# Revit family: BuroSeating_Konfurb Keen 5 Star
name_source: partatom
category: Furniture
units: mm (PartAtom-declared; Revit-internal decimal feet)

## family parameters
Always vertical = Yes
Cut with Voids When Loaded = No
OmniClass Number = 23.40.20.00
OmniClass Title = General Furniture and Specialties
Render Appearance Source = Family Geometry
Room Calculation Point = No
Shared = No
Work Plane-Based = No

## types (4) — shared parameters
Arm Finish = BuroSeating_Plastic_Black
Assembly Code = E2020
Back Finish = BuroSeating_Plastic_Navy
Base Finish = BuroSeating_Metal_PowderCoat_White
Caster Finish = BuroSeating_Plastic_Black
Cylinder Finish = BuroSeating_Metal_PowderCoat_White
Frame Finish = BuroSeating_Plastic_Silver
FrameMaterial = BuroSeating_Metal_PowderCoat_White
Glide Finish = BuroSeating_Plastic_Black
Leg Finish = BuroSeating_Plastic_Silver
Manufacturer = Buro Seating
Mechanism Finish = BuroSeating_Plastic_Black
ProductGroup = Konfurb Keen
ProductPageURL AU = https://buroseating.com
ProductRange = Konfurb
Ring Finish = BuroSeating_Metal_PowderCoat_White
Seat Finish = BuroSeating_Plastic_Navy
SeatDepth = 450 mm  [stored 1.47638 ft]
SeatWidth = 450 mm  [stored 1.47638 ft]
Supports Finish = BuroSeating_Plastic_Black
WarrantyDescription = Full 5 year guarantee (excluding upholstery)
zero-valued in all types: Default Elevation

## per-type parameters (varying)
| type | Arms | Description | Model | SeatHeight | Supports | Type Comments | URL | cacl_Cylinder | calc_ArmRest | calc_Number |
| PE388 - 5 Star | No | Chair stool, adjustable height, poly back and seat, Armless | PE388 | 600 mm | No | Standard | https://buroseating.com.au | 325 mm  [stored 1.06627 ft] | 455 mm | 1 |
| PE389 - 5 Star Architectural | No | Chair stool, adjustable height, poly back and seat, Armless | PE389 | 860 mm | Yes | Architectural | https://buroseating.co.nz | 600 mm | 600 mm | 3 |
| PE388 - 5 Star w Arms | Yes | Chair stool, adjustable height, poly back and seat, Arms | PE388 | 600 mm | No | Standard | https://buroseating.co.nz | 325 mm  [stored 1.06627 ft] | 455 mm | 2 |
| PE389 - 5 Star Architectural w Arms | Yes | Chair stool, adjustable height, poly back and seat, Arms | PE389 | 860 mm | Yes | Architectural | https://buroseating.co.nz | 600 mm | 600 mm | 4 |

note: [stored X ft] marks values corroborated as IEEE doubles in the binary element streams (Revit-internal decimal feet)

## geometry (parser evidence)
native form markers: Sweep x4
no freeform markers — native parametric forms only
